# Revit family: Basketball_Backstop-Outdoor-Ultimate_Fixed_Height-IPIbyBison-BA871-72
name_source: partatom
category: Specialty Equipment
units: mm (PartAtom-declared; Revit-internal decimal feet)

## family parameters
Always vertical = Yes
Cut with Voids When Loaded = No
Enable Cutting in Views = No
Maintain Annotation Orientation = No
OmniClass Number = 23.40.50.34.14
OmniClass Title = Gymnasium Equipment
Part Type = Normal
Room Calculation Point = No
Round Connector Dimension = Use Diameter
Shared = No
Work Plane-Based = No

## types (8) — shared parameters
Backboard Finish = Powder Coat - White
Backboard Height = 3' - 6"
Basket Netting = Finish - IPI by Bison - White Netting
CAD Details = https://www.arcat.com
Default Elevation = 0' - 0"
Description = Outdoor Basketball Frame and Backboard Systems
Embedding Depth = 4' - 0"
Hoop Elevation = 10' - 0"
Hoop Finish = Powder Coat - IPI by Bison - Outdoor Orange
Keynote = 11 66 00
Manufacturer = IPI by Bison
Post Height = 8' - 4"
Post Material = Steel - Galvanized - Hot Dipped
Post Square Width = 0' - 6"
Product Page URL = https://www.arcat.com
Specification = https://www.arcat.com
URL = https://ipibybison.com

## per-type parameters (varying)
| type | Backboard Length | Basket Type | Double Sided | Padding |
| BA871A-BK | 5' - 0" | BA39U | No | Padding - Black |
| BA871A-GV | 5' - 0" | BA39U-GV | No | Plastic - IPI by Bison - Scarlet SC |
| BA871-BK | 5' - 0" | BA39U | No | Plastic - IPI by Bison - Scarlet SC |
| BA872-BK | 5' - 0" | BA39U | Yes | Plastic - IPI by Bison - Scarlet SC |
| BA871XL-BK | 6' - 0" | BA39U | No | Plastic - IPI by Bison - Scarlet SC |
| BA872-GV | 5' - 0" | BA39U | Yes | Plastic - IPI by Bison - Scarlet SC |
| BA872A-BK | 5' - 0" | BA39U | Yes | Plastic - IPI by Bison - Scarlet SC |
| BA872XL-BK | 6' - 0" | BA39U | Yes | Plastic - IPI by Bison - Scarlet SC |

note: column(s) folded — value = type name in every type: Model

## geometry (parser evidence)
native form markers: Sweep x7
no freeform markers — native parametric forms only
